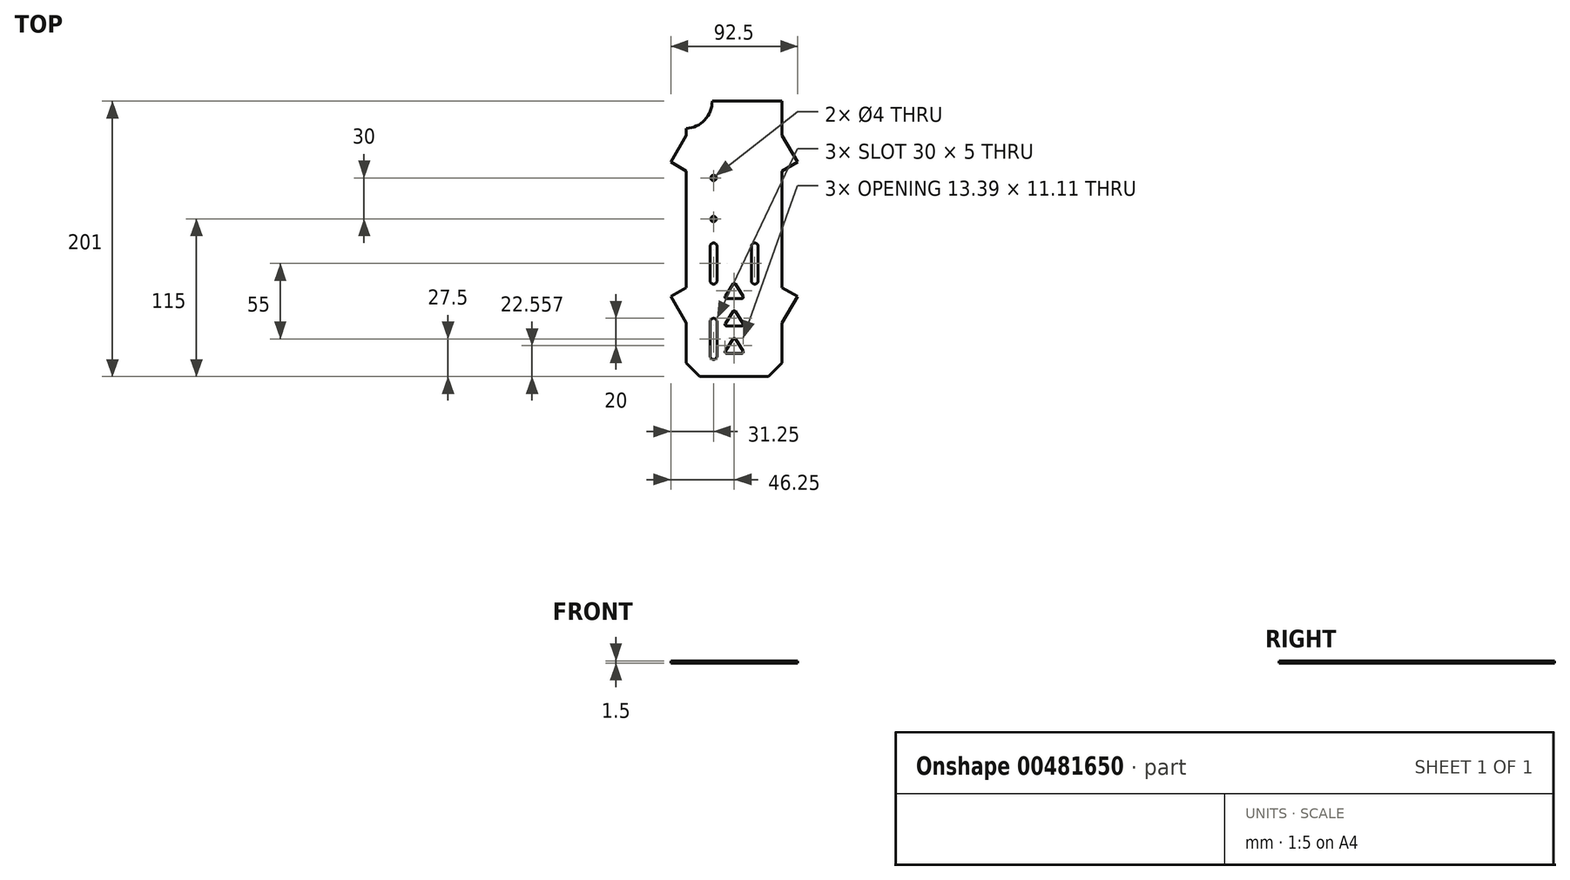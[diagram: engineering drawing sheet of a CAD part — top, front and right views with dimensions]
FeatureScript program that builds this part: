
annotation { "Feature Type Name" : "Feature", "Feature Type Description" : "" }
export const myFeature = defineFeature(function(context is Context, id is Id, definition is map)
    precondition{}
    {
        {
            var Q0;
            Q0=qCreatedBy(makeId("Top.planeOp"),FACE);
            var sketch = newSketch(context, id + "F0", { "sketchPlane" : qUnion([Q0])});
            skLineSegment(sketch, "E0.bottom", {"start": v(0, -100) * mm, "end": v(-25, -100) * mm});
            skLineSegment(sketch, "E0.top", {"start": v(0, 100) * mm, "end": v(-16, 100) * mm});
            skLineSegment(sketch, "E0.right", {"start": v(-35, -89) * mm, "end": v(-35, -65) * mm});
            skPoint(sketch, "E0.middle", {"position": v(0, 0) * mm});
            skArc(sketch, "E1", {"start": v(-35, 82) * mm, "mid": v(-23.6, 89) * mm, "end": v(-16, 100) * mm});
            skPoint(sketch, "E2", {"position": v(-35, 82) * mm});
            skPoint(sketch, "E3", {"position": v(-16, 100) * mm});
            skPoint(sketch, "E4.orphan", {"position": v(-35, 100) * mm});
            skLineSegment(sketch, "E5", {"start": v(0, -100) * mm, "end": v(0, 100) * mm, "construction": true});
            skLineSegment(sketch, "E6", {"start": v(-35, -89) * mm, "end": v(-25, -100) * mm});
            skPoint(sketch, "E7.orphan", {"position": v(-35, -100) * mm});
            skPoint(sketch, "E0.left.start.orphan", {"position": v(35, -100) * mm});
            skPoint(sketch, "E8.orphan", {"position": v(35, 100) * mm});
            skLineSegment(sketch, "E9", {"start": v(-35, -65) * mm, "end": v(-46, -45.95) * mm});
            skLineSegment(sketch, "E10", {"start": v(-35, -37) * mm, "end": v(-46, -45.95) * mm});
            skLineSegment(sketch, "E11.trimOffspring", {"start": v(-35, -37) * mm, "end": v(-35, 49) * mm});
            skLineSegment(sketch, "E12", {"start": v(-35, 49) * mm, "end": v(-45, 57.4) * mm});
            skLineSegment(sketch, "E13", {"start": v(-35, 77) * mm, "end": v(-45, 57.4) * mm});
            skLineSegment(sketch, "E14.trimOffspring", {"start": v(-35, 77) * mm, "end": v(-35, 82) * mm});
            skLineSegment(sketch, "E15.MirrorCS", {"start": v(0, 100) * mm, "end": v(16, 100) * mm});
            skArc(sketch, "E16.MirrorCS", {"start": v(35, 82) * mm, "mid": v(23.6, 89) * mm, "end": v(16, 100) * mm});
            skLineSegment(sketch, "E17.MirrorCS", {"start": v(35, 77) * mm, "end": v(35, 82) * mm});
            skLineSegment(sketch, "E18.MirrorCS", {"start": v(35, 77) * mm, "end": v(45, 57.4) * mm});
            skLineSegment(sketch, "E19.MirrorCS", {"start": v(35, 49) * mm, "end": v(45, 57.4) * mm});
            skLineSegment(sketch, "E20.MirrorCS", {"start": v(35, -37) * mm, "end": v(35, 49) * mm});
            skLineSegment(sketch, "E21.MirrorCS", {"start": v(35, -37) * mm, "end": v(46, -45.95) * mm});
            skLineSegment(sketch, "E22.MirrorCS", {"start": v(35, -65) * mm, "end": v(46, -45.95) * mm});
            skLineSegment(sketch, "E23.MirrorCS", {"start": v(35, -89) * mm, "end": v(35, -65) * mm});
            skLineSegment(sketch, "E24.MirrorCS", {"start": v(35, -89) * mm, "end": v(25, -100) * mm});
            skLineSegment(sketch, "E25.MirrorCS", {"start": v(0, -100) * mm, "end": v(25, -100) * mm});
            skSolve(sketch);
        }
        {
            var Q0;
            Q0=qCreatedBy(makeId("Top.planeOp"),FACE);
            var sketch = newSketch(context, id + "F1", { "sketchPlane" : qUnion([Q0])});
            skLineSegment(sketch, "E26.bottom", {"start": v(35, -100.5) * mm, "end": v(-35, -100.5) * mm});
            skLineSegment(sketch, "E26.top", {"start": v(35, 100.5) * mm, "end": v(-35, 100.5) * mm});
            skLineSegment(sketch, "E26.left", {"start": v(35, -100.5) * mm, "end": v(35, 100.5) * mm});
            skLineSegment(sketch, "E26.right", {"start": v(-35, -100.5) * mm, "end": v(-35, 100.5) * mm});
            skPoint(sketch, "E26.middle", {"position": v(0, 0) * mm});
            skLineSegment(sketch, "E27", {"start": v(35, -50.5) * mm, "end": v(88.1, -81.16) * mm, "construction": true});
            skLineSegment(sketch, "E28", {"start": v(35, 64.5) * mm, "end": v(86.63, 94.31) * mm, "construction": true});
            skLineSegment(sketch, "E29", {"start": v(33.25, 78.5) * mm, "end": v(35, 79.51) * mm});
            skLineSegment(sketch, "E30", {"start": v(35, 49.49) * mm, "end": v(46.25, 55.98) * mm});
            skLineSegment(sketch, "E31", {"start": v(35, -35.49) * mm, "end": v(46.25, -41.98) * mm});
            skLineSegment(sketch, "E32", {"start": v(33.25, -64.5) * mm, "end": v(35, -65.51) * mm});
            skLineSegment(sketch, "E33", {"start": v(46.25, 55.98) * mm, "end": v(33.25, 78.5) * mm});
            skLineSegment(sketch, "E34", {"start": v(46.25, -41.98) * mm, "end": v(33.25, -64.5) * mm});
            skPoint(sketch, "E34.endSnap0", {"position": v(40.62, -38.74) * mm});
            skLineSegment(sketch, "E35.MirrorCS", {"start": v(-33.25, -64.5) * mm, "end": v(-35, -65.51) * mm});
            skLineSegment(sketch, "E36.MirrorCS", {"start": v(-33.25, 78.5) * mm, "end": v(-35, 79.51) * mm});
            skLineSegment(sketch, "E37.MirrorCS", {"start": v(-35, -35.49) * mm, "end": v(-46.25, -41.98) * mm});
            skLineSegment(sketch, "E38.MirrorCS", {"start": v(-35, 49.49) * mm, "end": v(-46.25, 55.98) * mm});
            skPoint(sketch, "E39.MirrorP", {"position": v(-40.62, -38.74) * mm});
            skLineSegment(sketch, "E40.MirrorCS", {"start": v(-46.25, 55.98) * mm, "end": v(-33.25, 78.5) * mm});
            skLineSegment(sketch, "E41.MirrorCS", {"start": v(-46.25, -41.98) * mm, "end": v(-33.25, -64.5) * mm});
            skSolve(sketch);
        }
        {
            var Q0;
            {var subQ1=sQuery(id+"F1.wireOp",EDGE,"E26.bottom");Q0=makeQuery(id+"F1.imprint","IMPRINT",FACE,{"disambiguationData":[TD([[makeQuery(id+"F1.imprint","IMPRINT",EDGE,{"derivedFrom":subQ1}),-1.0]])]});}
            var Q1;
            {var subQ0=sQuery(id+"F1.wireOp",EDGE,"E38.MirrorCS");Q1=makeQuery(id+"F1.imprint","IMPRINT",FACE,{"disambiguationData":[TD([[makeQuery(id+"F1.imprint","IMPRINT",EDGE,{"derivedFrom":subQ0}),-1.0]])]});}
            var Q2;
            {var subQ0=sQuery(id+"F1.wireOp",EDGE,"E30");Q2=makeQuery(id+"F1.imprint","IMPRINT",FACE,{"disambiguationData":[TD([[makeQuery(id+"F1.imprint","IMPRINT",EDGE,{"derivedFrom":subQ0}),1.0]])]});}
            var Q3;
            {var subQ0=sQuery(id+"F1.wireOp",EDGE,"E31");Q3=makeQuery(id+"F1.imprint","IMPRINT",FACE,{"disambiguationData":[TD([[makeQuery(id+"F1.imprint","IMPRINT",EDGE,{"derivedFrom":subQ0}),-1.0]])]});}
            var Q4;
            {var subQ0=sQuery(id+"F1.wireOp",EDGE,"E37.MirrorCS");Q4=makeQuery(id+"F1.imprint","IMPRINT",FACE,{"disambiguationData":[TD([[makeQuery(id+"F1.imprint","IMPRINT",EDGE,{"derivedFrom":subQ0}),1.0]])]});}
            var Q5;
            {var subQ0=sQuery(id+"F1.wireOp",EDGE,"E36.MirrorCS");Q5=makeQuery(id+"F1.imprint","IMPRINT",FACE,{"disambiguationData":[TD([[makeQuery(id+"F1.imprint","IMPRINT",EDGE,{"derivedFrom":subQ0}),1.0]])]});}
            var Q6;
            {var subQ0=sQuery(id+"F1.wireOp",EDGE,"E29");Q6=makeQuery(id+"F1.imprint","IMPRINT",FACE,{"disambiguationData":[TD([[makeQuery(id+"F1.imprint","IMPRINT",EDGE,{"derivedFrom":subQ0}),-1.0]])]});}
            var Q7;
            {var subQ0=sQuery(id+"F1.wireOp",EDGE,"E32");Q7=makeQuery(id+"F1.imprint","IMPRINT",FACE,{"disambiguationData":[TD([[makeQuery(id+"F1.imprint","IMPRINT",EDGE,{"derivedFrom":subQ0}),1.0]])]});}
            var Q8;
            {var subQ0=sQuery(id+"F1.wireOp",EDGE,"E35.MirrorCS");Q8=makeQuery(id+"F1.imprint","IMPRINT",FACE,{"disambiguationData":[TD([[makeQuery(id+"F1.imprint","IMPRINT",EDGE,{"derivedFrom":subQ0}),-1.0]])]});}
            extrude(context, id + "F2", {"entities" : qUnion([Q0, Q1, Q2, Q3, Q4, Q5, Q6, Q7, Q8]), "depth" : 1.5 * mm, "offsetDistance" : 25 * mm});
        }
        {
            var Q0;
            Q0=makeQuery(id+"F2.opExtrude","CAP_FACE",FACE,{"disambiguationData":[OSD([sQuery(id+"F1.wireOp",EDGE,"E26.bottom"),sQuery(id+"F1.wireOp",EDGE,"E26.top"),sQuery(id+"F1.wireOp",EDGE,"E26.left"),sQuery(id+"F1.wireOp",EDGE,"E26.right"),sQuery(id+"F1.wireOp",EDGE,"E29"),sQuery(id+"F1.wireOp",EDGE,"E30"),sQuery(id+"F1.wireOp",EDGE,"E31"),sQuery(id+"F1.wireOp",EDGE,"E32"),sQuery(id+"F1.wireOp",EDGE,"E33"),sQuery(id+"F1.wireOp",EDGE,"E34"),sQuery(id+"F1.wireOp",EDGE,"E35.MirrorCS"),sQuery(id+"F1.wireOp",EDGE,"E36.MirrorCS"),sQuery(id+"F1.wireOp",EDGE,"E37.MirrorCS"),sQuery(id+"F1.wireOp",EDGE,"E38.MirrorCS"),sQuery(id+"F1.wireOp",EDGE,"E40.MirrorCS"),sQuery(id+"F1.wireOp",EDGE,"E41.MirrorCS")])],"isStart":false});
            var sketch = newSketch(context, id + "F3", { "sketchPlane" : qUnion([Q0])});
            skLineSegment(sketch, "E42", {"start": v(0, 100.5) * mm, "end": v(-16, 100.5) * mm});
            skCircle(sketch, "E43", {"center": v(-36, 100.5) * mm, "radius": 20 * mm});
            skLineSegment(sketch, "E44", {"start": v(-35, -90.5) * mm, "end": v(-25, -100.5) * mm});
            skLineSegment(sketch, "E45", {"start": v(-25, -100.5) * mm, "end": v(-35, -100.5) * mm});
            skLineSegment(sketch, "E46", {"start": v(-35, -100.5) * mm, "end": v(-35, -90.5) * mm});
            skLineSegment(sketch, "E47", {"start": v(-15, -85.5) * mm, "end": v(-15, -60.5) * mm, "construction": true});
            skArc(sketch, "E48", {"start": v(-12.5, -60.5) * mm, "mid": v(-15, -58) * mm, "end": v(-17.5, -60.5) * mm});
            skArc(sketch, "E49", {"start": v(-17.5, -85.5) * mm, "mid": v(-15, -88) * mm, "end": v(-12.5, -85.5) * mm});
            skLineSegment(sketch, "E50", {"start": v(-12.5, -60.5) * mm, "end": v(-12.5, -85.5) * mm});
            skLineSegment(sketch, "E51", {"start": v(-17.5, -60.5) * mm, "end": v(-17.5, -85.5) * mm});
            skLineSegment(sketch, "E52", {"start": v(-21.89, -45.5) * mm, "end": v(-9.75, -45.5) * mm, "construction": true});
            skArc(sketch, "E53.MirrorCS", {"start": v(-17.5, -60.5) * mm, "mid": v(-15, -58) * mm, "end": v(-12.5, -60.5) * mm});
            skArc(sketch, "E54.MirrorCS", {"start": v(-12.5, -85.5) * mm, "mid": v(-15, -88) * mm, "end": v(-17.5, -85.5) * mm});
            skLineSegment(sketch, "E55.MirrorCS", {"start": v(-12.5, -30.5) * mm, "end": v(-12.5, -5.5) * mm});
            skArc(sketch, "E56.MirrorCS", {"start": v(-12.5, -5.5) * mm, "mid": v(-15, -3) * mm, "end": v(-17.5, -5.5) * mm});
            skArc(sketch, "E57.MirrorCS", {"start": v(-17.5, -30.5) * mm, "mid": v(-15, -33) * mm, "end": v(-12.5, -30.5) * mm});
            skLineSegment(sketch, "E58.MirrorCS", {"start": v(-17.5, -30.5) * mm, "end": v(-17.5, -5.5) * mm});
            skArc(sketch, "E59.MirrorCS", {"start": v(-12.5, -30.5) * mm, "mid": v(-15, -33) * mm, "end": v(-17.5, -30.5) * mm});
            skArc(sketch, "E60.MirrorCS", {"start": v(-17.5, -5.5) * mm, "mid": v(-15, -3) * mm, "end": v(-12.5, -5.5) * mm});
            skLineSegment(sketch, "E61.MirrorCS", {"start": v(-15, -5.5) * mm, "end": v(-15, -30.5) * mm, "construction": true});
            skArc(sketch, "E62.MirrorCS", {"start": v(12.5, -30.5) * mm, "mid": v(15, -33) * mm, "end": v(17.5, -30.5) * mm});
            skArc(sketch, "E63.MirrorCS", {"start": v(17.5, -60.5) * mm, "mid": v(15, -58) * mm, "end": v(12.5, -60.5) * mm});
            skArc(sketch, "E64.MirrorCS", {"start": v(12.5, -85.5) * mm, "mid": v(15, -88) * mm, "end": v(17.5, -85.5) * mm});
            skArc(sketch, "E65.MirrorCS", {"start": v(12.5, -5.5) * mm, "mid": v(15, -3) * mm, "end": v(17.5, -5.5) * mm});
            skArc(sketch, "E66.MirrorCS", {"start": v(12.5, -60.5) * mm, "mid": v(15, -58) * mm, "end": v(17.5, -60.5) * mm});
            skArc(sketch, "E67.MirrorCS", {"start": v(17.5, -30.5) * mm, "mid": v(15, -33) * mm, "end": v(12.5, -30.5) * mm});
            skArc(sketch, "E68.MirrorCS", {"start": v(17.5, -5.5) * mm, "mid": v(15, -3) * mm, "end": v(12.5, -5.5) * mm});
            skArc(sketch, "E69.MirrorCS", {"start": v(17.5, -85.5) * mm, "mid": v(15, -88) * mm, "end": v(12.5, -85.5) * mm});
            skLineSegment(sketch, "E70.MirrorCS", {"start": v(17.5, -30.5) * mm, "end": v(17.5, -5.5) * mm});
            skLineSegment(sketch, "E71.MirrorCS", {"start": v(12.5, -60.5) * mm, "end": v(12.5, -85.5) * mm});
            skLineSegment(sketch, "E72.MirrorCS", {"start": v(17.5, -60.5) * mm, "end": v(17.5, -85.5) * mm});
            skLineSegment(sketch, "E73.MirrorCS", {"start": v(12.5, -30.5) * mm, "end": v(12.5, -5.5) * mm});
            skLineSegment(sketch, "E74.MirrorCS", {"start": v(15, -5.5) * mm, "end": v(15, -30.5) * mm, "construction": true});
            skLineSegment(sketch, "E75.MirrorCS", {"start": v(21.89, -45.5) * mm, "end": v(9.75, -45.5) * mm, "construction": true});
            skLineSegment(sketch, "E76.MirrorCS", {"start": v(15, -85.5) * mm, "end": v(15, -60.5) * mm, "construction": true});
            skLineSegment(sketch, "E77.MirrorCS", {"start": v(35, -100.5) * mm, "end": v(35, -90.5) * mm});
            skLineSegment(sketch, "E78.MirrorCS", {"start": v(25, -100.5) * mm, "end": v(35, -100.5) * mm});
            skLineSegment(sketch, "E79.MirrorCS", {"start": v(35, -90.5) * mm, "end": v(25, -100.5) * mm});
            skCircle(sketch, "E80.MirrorC", {"center": v(36, 100.5) * mm, "radius": 20 * mm});
            skLineSegment(sketch, "E81", {"start": v(-5.7, -83.5) * mm, "end": v(0, -83.5) * mm});
            skLineSegment(sketch, "E82", {"start": v(-6.54, -81.97) * mm, "end": v(-0.85, -72.86) * mm});
            skLineSegment(sketch, "E83.MirrorCS", {"start": v(6.54, -81.97) * mm, "end": v(0.85, -72.86) * mm});
            skLineSegment(sketch, "E84.MirrorCS", {"start": v(5.7, -83.5) * mm, "end": v(0, -83.5) * mm});
            skPoint(sketch, "E85.visualSharp", {"position": v(0, -71.5) * mm});
            skArc(sketch, "E85.filletArc", {"start": v(0.85, -72.86) * mm, "mid": v(0, -72.39) * mm, "end": v(-0.85, -72.86) * mm});
            skPoint(sketch, "E86.visualSharp", {"position": v(-7.5, -83.5) * mm});
            skArc(sketch, "E86.filletArc", {"start": v(-6.54, -81.97) * mm, "mid": v(-6.57, -82.98) * mm, "end": v(-5.7, -83.5) * mm});
            skPoint(sketch, "E87.visualSharp", {"position": v(7.5, -83.5) * mm});
            skArc(sketch, "E87.filletArc", {"start": v(5.7, -83.5) * mm, "mid": v(6.57, -82.98) * mm, "end": v(6.54, -81.97) * mm});
            skLineSegment(sketch, "E88.0.1.0", {"start": v(5.7, -63.5) * mm, "end": v(0, -63.5) * mm});
            skPoint(sketch, "E88.0.1.1", {"position": v(0, -51.5) * mm});
            skLineSegment(sketch, "E88.0.1.2", {"start": v(6.54, -61.97) * mm, "end": v(0.85, -52.86) * mm});
            skLineSegment(sketch, "E88.0.1.3", {"start": v(-6.54, -61.97) * mm, "end": v(-0.85, -52.86) * mm});
            skLineSegment(sketch, "E88.0.1.4", {"start": v(-5.7, -63.5) * mm, "end": v(0, -63.5) * mm});
            skPoint(sketch, "E88.0.1.5", {"position": v(-7.5, -63.5) * mm});
            skPoint(sketch, "E88.0.1.6", {"position": v(7.5, -63.5) * mm});
            skArc(sketch, "E88.0.1.7", {"start": v(0.85, -52.86) * mm, "mid": v(0, -52.39) * mm, "end": v(-0.85, -52.86) * mm});
            skArc(sketch, "E88.0.1.8", {"start": v(-6.54, -61.97) * mm, "mid": v(-6.57, -62.98) * mm, "end": v(-5.7, -63.5) * mm});
            skArc(sketch, "E88.0.1.9", {"start": v(5.7, -63.5) * mm, "mid": v(6.57, -62.98) * mm, "end": v(6.54, -61.97) * mm});
            skLineSegment(sketch, "E88.0.2.0", {"start": v(5.7, -43.5) * mm, "end": v(0, -43.5) * mm});
            skPoint(sketch, "E88.0.2.1", {"position": v(0, -31.5) * mm});
            skLineSegment(sketch, "E88.0.2.2", {"start": v(6.54, -41.97) * mm, "end": v(0.85, -32.86) * mm});
            skLineSegment(sketch, "E88.0.2.3", {"start": v(-6.54, -41.97) * mm, "end": v(-0.85, -32.86) * mm});
            skLineSegment(sketch, "E88.0.2.4", {"start": v(-5.7, -43.5) * mm, "end": v(0, -43.5) * mm});
            skPoint(sketch, "E88.0.2.5", {"position": v(-7.5, -43.5) * mm});
            skPoint(sketch, "E88.0.2.6", {"position": v(7.5, -43.5) * mm});
            skArc(sketch, "E88.0.2.7", {"start": v(0.85, -32.86) * mm, "mid": v(0, -32.39) * mm, "end": v(-0.85, -32.86) * mm});
            skArc(sketch, "E88.0.2.8", {"start": v(-6.54, -41.97) * mm, "mid": v(-6.57, -42.98) * mm, "end": v(-5.7, -43.5) * mm});
            skArc(sketch, "E88.0.2.9", {"start": v(5.7, -43.5) * mm, "mid": v(6.57, -42.98) * mm, "end": v(6.54, -41.97) * mm});
            skLineSegment(sketch, "E88.direction1", {"start": v(-7.5, -83.5) * mm, "end": v(18.6, -83.5) * mm, "construction": true});
            skLineSegment(sketch, "E88.direction2", {"start": v(-7.5, -83.5) * mm, "end": v(-7.5, -63.5) * mm, "construction": true});
            skCircle(sketch, "E89", {"center": v(-15, 14.5) * mm, "radius": 2 * mm});
            skCircle(sketch, "E90", {"center": v(-15, 44.5) * mm, "radius": 2 * mm});
            skCircle(sketch, "E91.MirrorC", {"center": v(15, 14.5) * mm, "radius": 2 * mm});
            skCircle(sketch, "E92.MirrorC", {"center": v(15, 44.5) * mm, "radius": 2 * mm});
            skSolve(sketch);
        }
        {
            var Q0;
            Q0=makeQuery(id+"F3.imprint","IMPRINT",FACE,{"disambiguationData":[TD([[makeQuery(id+"F3.imprint","IMPRINT",EDGE,{"derivedFrom":sQuery(id+"F3.wireOp",EDGE,"E44")}),-1.0]])]});
            var Q1;
            Q1=makeQuery(id+"F3.imprint","IMPRINT",FACE,{"disambiguationData":[TD([[makeQuery(id+"F3.imprint","IMPRINT",EDGE,{"derivedFrom":sQuery(id+"F3.wireOp",EDGE,"E49")}),1.0]])]});
            var Q2;
            Q2=makeQuery(id+"F3.imprint","IMPRINT",FACE,{"disambiguationData":[TD([[makeQuery(id+"F3.imprint","IMPRINT",EDGE,{"derivedFrom":sQuery(id+"F3.wireOp",EDGE,"E55.MirrorCS")}),1.0]])]});
            var Q3;
            Q3=makeQuery(id+"F3.imprint","IMPRINT",FACE,{"disambiguationData":[TD([[makeQuery(id+"F3.imprint","IMPRINT",EDGE,{"derivedFrom":sQuery(id+"F3.wireOp",EDGE,"E66.MirrorCS")}),-1.0]])]});
            var Q4;
            Q4=makeQuery(id+"F3.imprint","IMPRINT",FACE,{"disambiguationData":[TD([[makeQuery(id+"F3.imprint","IMPRINT",EDGE,{"derivedFrom":sQuery(id+"F3.wireOp",EDGE,"E62.MirrorCS")}),1.0]])]});
            var Q5;
            Q5=makeQuery(id+"F3.imprint","IMPRINT",FACE,{"disambiguationData":[TD([[makeQuery(id+"F3.imprint","IMPRINT",EDGE,{"derivedFrom":sQuery(id+"F3.wireOp",EDGE,"E77.MirrorCS")}),1.0]])]});
            var Q6;
            Q6=makeQuery(id+"F3.imprint","IMPRINT",FACE,{"disambiguationData":[TD([[makeQuery(id+"F3.imprint","IMPRINT",EDGE,{"derivedFrom":sQuery(id+"F3.wireOp",EDGE,"E81")}),1.0]])]});
            var Q7;
            Q7=makeQuery(id+"F3.imprint","IMPRINT",FACE,{"disambiguationData":[TD([[makeQuery(id+"F3.imprint","IMPRINT",EDGE,{"derivedFrom":sQuery(id+"F3.wireOp",EDGE,"E88.0.1.0")}),-1.0]])]});
            var Q8;
            Q8=makeQuery(id+"F3.imprint","IMPRINT",FACE,{"disambiguationData":[TD([[makeQuery(id+"F3.imprint","IMPRINT",EDGE,{"derivedFrom":sQuery(id+"F3.wireOp",EDGE,"E88.0.2.0")}),-1.0]])]});
            var Q9;
            Q9=makeQuery(id+"F3.imprint","IMPRINT",FACE,{"disambiguationData":[TD([[makeQuery(id+"F3.imprint","IMPRINT",EDGE,{"derivedFrom":sQuery(id+"F3.wireOp",EDGE,"E89")}),1.0]])]});
            var Q10;
            Q10=makeQuery(id+"F3.imprint","IMPRINT",FACE,{"disambiguationData":[TD([[makeQuery(id+"F3.imprint","IMPRINT",EDGE,{"derivedFrom":sQuery(id+"F3.wireOp",EDGE,"E90")}),1.0]])]});
            var Q11;
            Q11=makeQuery(id+"F3.imprint","IMPRINT",FACE,{"disambiguationData":[TD([[makeQuery(id+"F3.imprint","IMPRINT",EDGE,{"derivedFrom":sQuery(id+"F3.wireOp",EDGE,"E91.MirrorC")}),-1.0]])]});
            var Q12;
            Q12=makeQuery(id+"F3.imprint","IMPRINT",FACE,{"disambiguationData":[TD([[makeQuery(id+"F3.imprint","IMPRINT",EDGE,{"derivedFrom":sQuery(id+"F3.wireOp",EDGE,"E92.MirrorC")}),-1.0]])]});
            var Q13;
            {var subQ0=sQuery(id+"F3.wireOp",EDGE,"E43");var subQ1=sQuery(id+"F1.wireOp",EDGE,"E26.top");var subQ2=makeQuery(id+"F2.opExtrude","CAP_EDGE",EDGE,{"disambiguationData":[OSD([subQ1])],"isStart":false});var subQ3=makeQuery(id+"F3.imprint","INTERSECT",VERTEX,{"derivedFrom":[subQ2,sQuery(id+"F3.wireOp",EDGE,"E42"),subQ0]});Q13=makeQuery(id+"F3.imprint","IMPRINT",FACE,{"disambiguationData":[TD([[makeQuery(id+"F3.imprint","IMPRINT",EDGE,{"disambiguationData":[TD([[subQ3,-1.0]])],"derivedFrom":subQ0}),1.0]])]});}
            var Q14;
            {var subQ0=sQuery(id+"F3.wireOp",EDGE,"E80.MirrorC");var subQ1=sQuery(id+"F1.wireOp",EDGE,"E26.top");var subQ2=makeQuery(id+"F2.opExtrude","CAP_EDGE",EDGE,{"disambiguationData":[OSD([subQ1])],"isStart":false});var subQ3=makeQuery(id+"F3.imprint","INTERSECT",VERTEX,{"derivedFrom":[subQ2,subQ0]});Q14=makeQuery(id+"F3.imprint","IMPRINT",FACE,{"disambiguationData":[TD([[makeQuery(id+"F3.imprint","IMPRINT",EDGE,{"disambiguationData":[TD([[subQ3,-1.0]])],"derivedFrom":subQ0}),-1.0]])]});}
            var Q15;
            {var subQ0=sQuery(id+"F3.wireOp",EDGE,"E80.MirrorC");var subQ1=sQuery(id+"F1.wireOp",EDGE,"E26.top");var subQ2=makeQuery(id+"F2.opExtrude","CAP_EDGE",EDGE,{"disambiguationData":[OSD([subQ1])],"isStart":false});var subQ3=makeQuery(id+"F3.imprint","INTERSECT",VERTEX,{"derivedFrom":[subQ2,subQ0]});Q15=makeQuery(id+"F3.imprint","IMPRINT",FACE,{"disambiguationData":[TD([[makeQuery(id+"F3.imprint","IMPRINT",EDGE,{"disambiguationData":[TD([[subQ3,1.0]])],"derivedFrom":subQ0}),-1.0]])]});}
            var Q16;
            {var subQ0=sQuery(id+"F3.wireOp",EDGE,"E43");var subQ1=sQuery(id+"F1.wireOp",EDGE,"E26.top");var subQ2=makeQuery(id+"F2.opExtrude","CAP_EDGE",EDGE,{"disambiguationData":[OSD([subQ1])],"isStart":false});var subQ3=makeQuery(id+"F3.imprint","INTERSECT",VERTEX,{"derivedFrom":[subQ2,sQuery(id+"F3.wireOp",EDGE,"E42"),subQ0]});Q16=makeQuery(id+"F3.imprint","IMPRINT",FACE,{"disambiguationData":[TD([[makeQuery(id+"F3.imprint","IMPRINT",EDGE,{"disambiguationData":[TD([[subQ3,1.0]])],"derivedFrom":subQ0}),1.0]])]});}
            extrude(context, id + "F4", {"entities" : qUnion([Q0, Q1, Q2, Q3, Q4, Q5, Q6, Q7, Q8, Q9, Q10, Q11, Q12, Q13, Q14, Q15, Q16]), "operationType" : NewBodyOperationType.REMOVE, "oppositeDirection" : true, "depth" : 25 * mm, "offsetDistance" : 25 * mm});
        }
    });
